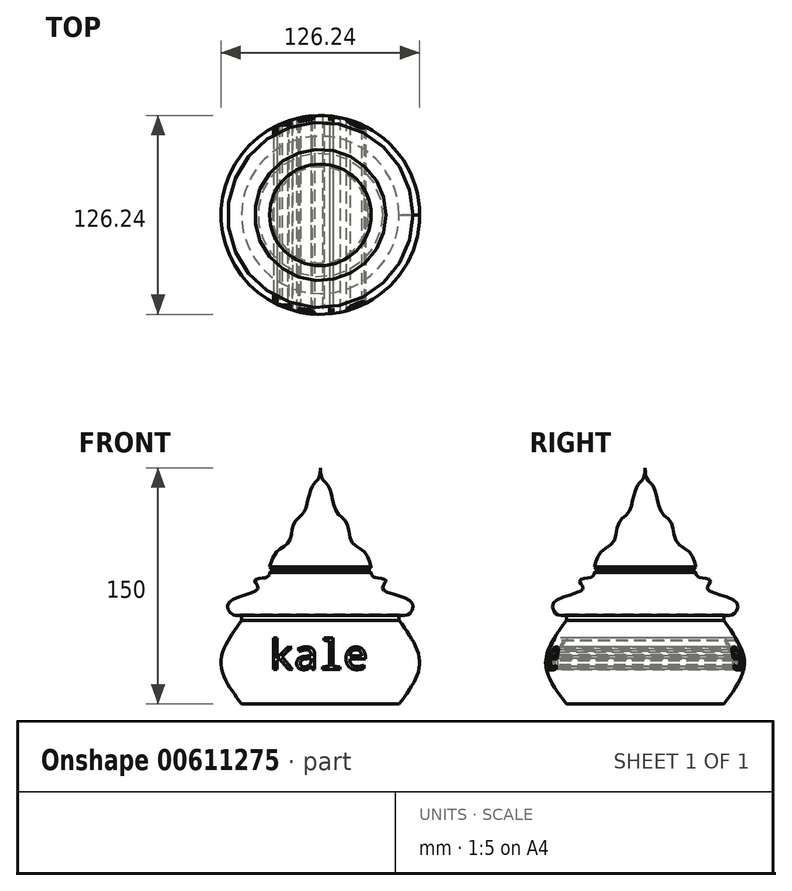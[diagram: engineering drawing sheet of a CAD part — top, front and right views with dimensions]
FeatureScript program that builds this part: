
annotation { "Feature Type Name" : "Feature", "Feature Type Description" : "" }
export const myFeature = defineFeature(function(context is Context, id is Id, definition is map)
    precondition{}
    {
        {
            var Q0;
            Q0=qCreatedBy(makeId("Front.planeOp"),FACE);
            var sketch = newSketch(context, id + "F0", { "sketchPlane" : qUnion([Q0])});
            skLineSegment(sketch, "E0", {"start": v(0, 75) * mm, "end": v(0, -75) * mm});
            skLineSegment(sketch, "E1", {"start": v(0, -75) * mm, "end": v(50, -75) * mm});
            skFitSpline(sketch, "E2", {"points": [v(50, -75) * mm, v(63.12, -48.94) * mm, v(50, -21.97) * mm], "startDerivative": vector(39.45, 52.2) * mm, "endDerivative": vector(-39.27, 53.85) * mm});
            skLineSegment(sketch, "E3", {"start": v(50, -21.97) * mm, "end": v(50, -18.04) * mm});
            skFitSpline(sketch, "E4", {"points": [v(50, -18.04) * mm, v(56.03, -18.04) * mm, v(57.9, -10.4) * mm, v(39.53, -1.7) * mm, v(41.71, 3.45) * mm, v(35.28, 5.1) * mm, v(33.25, 6.22) * mm, v(32.25, 8.44) * mm], "startDerivative": vector(45.06, -12.91) * mm, "endDerivative": vector(12.16, 28.98) * mm});
            skLineSegment(sketch, "E5", {"start": v(32.25, 8.44) * mm, "end": v(30.51, 9.7) * mm});
            skLineSegment(sketch, "E6", {"start": v(30.51, 9.7) * mm, "end": v(32.25, 12.08) * mm});
            skFitSpline(sketch, "E7", {"points": [v(32.25, 12.08) * mm, v(27.74, 21.77) * mm, v(19.8, 28.34) * mm, v(16.65, 40.13) * mm, v(10.89, 46.15) * mm, v(7.48, 56.1) * mm, v(4.34, 64.48) * mm, v(1.09, 68.05) * mm, v(0, 75) * mm], "startDerivative": vector(-22.72, 79.85) * mm, "endDerivative": vector(-1.87, 71.25) * mm});
            skSolve(sketch);
        }
        {
            var Q0;
            Q0=makeQuery(id+"F0.imprint","IMPRINT",FACE,{"disambiguationData":[TD([[makeQuery(id+"F0.imprint","IMPRINT",EDGE,{"derivedFrom":sQuery(id+"F0.wireOp",EDGE,"E0")}),1.0]])]});
            var Q1;
            Q1=sQuery(id+"F0.wireOp",EDGE,"E0");
            revolve(context, id + "F1", {"entities" : qUnion([Q0]), "axis" : qUnion([Q1]), "revolveType" : RevolveType.FULL});
        }
        {
            var Q0;
            Q0=qCreatedBy(makeId("Front.planeOp"),FACE);
            var sketch = newSketch(context, id + "F2", { "sketchPlane" : qUnion([Q0])});
            skText(sketch, "E8", { "text": "kale", "fontName": "DroidSansMono.ttf"});
            const initialGuessF2  = {"E8": [-0.0325, -0.053, 1, 0, 0.01883]};
            skSetInitialGuess(sketch, initialGuessF2);
            skSolve(sketch);
        }
        {
            var Q0;
            Q0 = qSketchRegion(id + "F2", true);
            extrude(context, id + "F3", {"entities" : qUnion([Q0]), "operationType" : NewBodyOperationType.REMOVE, "endBound" : BoundingType.SYMMETRIC, "oppositeDirection" : true, "depth" : 228.4 * mm, "offsetDistance" : 25 * mm});
        }
    });
